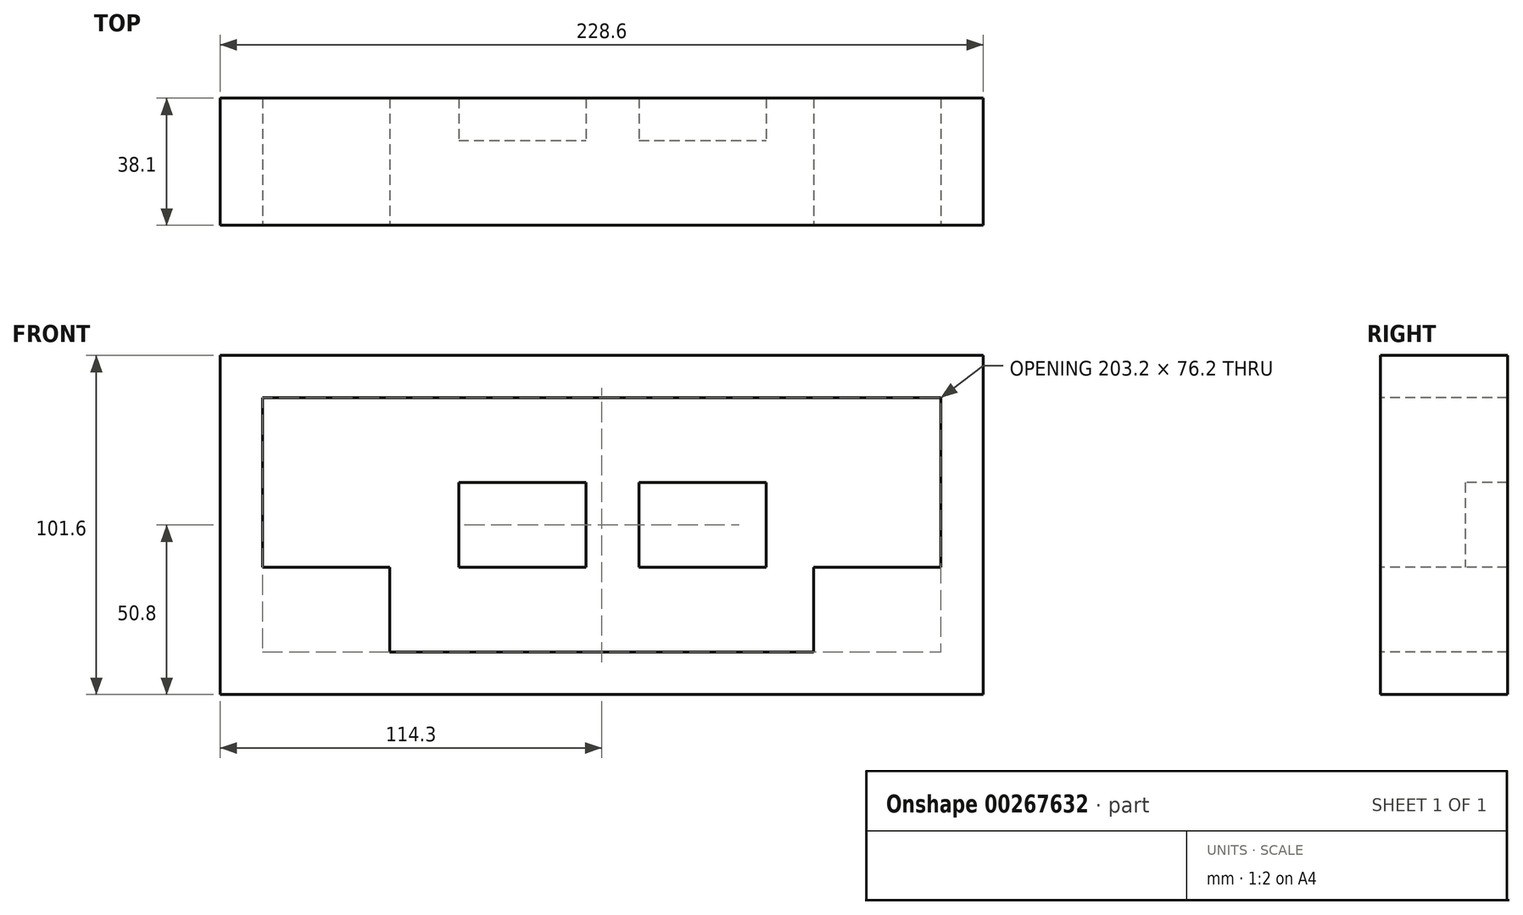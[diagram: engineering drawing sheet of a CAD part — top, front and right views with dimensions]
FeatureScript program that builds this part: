
annotation { "Feature Type Name" : "Feature", "Feature Type Description" : "" }
export const myFeature = defineFeature(function(context is Context, id is Id, definition is map)
    precondition{}
    {
        {
            var Q0;
            Q0=qCreatedBy(makeId("Front.planeOp"),FACE);
            var sketch = newSketch(context, id + "F0", { "sketchPlane" : qUnion([Q0])});
            skPoint(sketch, "E0.middle", {"position": v(0, 0) * mm});
            skLineSegment(sketch, "E1.bottom", {"start": v(-114.3, -50.8) * mm, "end": v(114.3, -50.8) * mm});
            skLineSegment(sketch, "E1.top", {"start": v(-114.3, 50.8) * mm, "end": v(114.3, 50.8) * mm});
            skLineSegment(sketch, "E1.left", {"start": v(-114.3, -50.8) * mm, "end": v(-114.3, 50.8) * mm});
            skLineSegment(sketch, "E1.right", {"start": v(114.3, -50.8) * mm, "end": v(114.3, 50.8) * mm});
            skLineSegment(sketch, "E2.bottom", {"start": v(-101.6, -38.1) * mm, "end": v(101.6, -38.1) * mm});
            skLineSegment(sketch, "E2.top", {"start": v(-101.6, 38.1) * mm, "end": v(101.6, 38.1) * mm});
            skLineSegment(sketch, "E2.left", {"start": v(-101.6, -38.1) * mm, "end": v(-101.6, 38.1) * mm});
            skLineSegment(sketch, "E2.right", {"start": v(101.6, -38.1) * mm, "end": v(101.6, 38.1) * mm});
            skLineSegment(sketch, "E3.bottom", {"start": v(-101.6, 38.1) * mm, "end": v(-62.18, 38.1) * mm});
            skLineSegment(sketch, "E3.top", {"start": v(-101.6, 12.7) * mm, "end": v(-62.18, 12.7) * mm});
            skLineSegment(sketch, "E3.left", {"start": v(-101.6, 38.1) * mm, "end": v(-101.6, 12.7) * mm});
            skLineSegment(sketch, "E3.right", {"start": v(-62.18, 38.1) * mm, "end": v(-62.18, 12.7) * mm});
            skLineSegment(sketch, "E4.bottom", {"start": v(-101.6, -38.1) * mm, "end": v(-63.5, -38.1) * mm});
            skLineSegment(sketch, "E4.top", {"start": v(-101.6, -12.7) * mm, "end": v(-63.5, -12.7) * mm});
            skLineSegment(sketch, "E4.left", {"start": v(-101.6, -38.1) * mm, "end": v(-101.6, -12.7) * mm});
            skLineSegment(sketch, "E4.right", {"start": v(-63.5, -38.1) * mm, "end": v(-63.5, -12.7) * mm});
            skLineSegment(sketch, "E5.bottom", {"start": v(101.6, -38.1) * mm, "end": v(63.5, -38.1) * mm});
            skLineSegment(sketch, "E5.top", {"start": v(101.6, -12.7) * mm, "end": v(63.5, -12.7) * mm});
            skLineSegment(sketch, "E5.left", {"start": v(101.6, -38.1) * mm, "end": v(101.6, -12.7) * mm});
            skLineSegment(sketch, "E5.right", {"start": v(63.5, -38.1) * mm, "end": v(63.5, -12.7) * mm});
            skLineSegment(sketch, "E6.bottom", {"start": v(101.6, 38.1) * mm, "end": v(63.5, 38.1) * mm});
            skLineSegment(sketch, "E6.top", {"start": v(101.6, 12.7) * mm, "end": v(63.5, 12.7) * mm});
            skLineSegment(sketch, "E6.left", {"start": v(101.6, 38.1) * mm, "end": v(101.6, 12.7) * mm});
            skLineSegment(sketch, "E6.right", {"start": v(63.5, 38.1) * mm, "end": v(63.5, 12.7) * mm});
            skLineSegment(sketch, "E7.bottom", {"start": v(-42.84, 12.7) * mm, "end": v(-4.74, 12.7) * mm});
            skLineSegment(sketch, "E7.top", {"start": v(-42.84, -12.7) * mm, "end": v(-4.74, -12.7) * mm});
            skLineSegment(sketch, "E7.left", {"start": v(-42.84, 12.7) * mm, "end": v(-42.84, -12.7) * mm});
            skLineSegment(sketch, "E7.right", {"start": v(-4.74, 12.7) * mm, "end": v(-4.74, -12.7) * mm});
            skPoint(sketch, "E7.middle", {"position": v(-23.8, 0) * mm});
            skLineSegment(sketch, "E8.bottom", {"start": v(11.17, 12.7) * mm, "end": v(49.27, 12.7) * mm});
            skLineSegment(sketch, "E8.top", {"start": v(11.17, -12.7) * mm, "end": v(49.27, -12.7) * mm});
            skLineSegment(sketch, "E8.left", {"start": v(11.17, 12.7) * mm, "end": v(11.17, -12.7) * mm});
            skLineSegment(sketch, "E8.right", {"start": v(49.27, 12.7) * mm, "end": v(49.27, -12.7) * mm});
            skPoint(sketch, "E8.middle", {"position": v(30.22, 0) * mm});
            skSolve(sketch);
        }
        {
            var Q0;
            Q0=makeQuery(id+"F0.imprint","IMPRINT",FACE,{"disambiguationData":[TD([[makeQuery(id+"F0.imprint","IMPRINT",EDGE,{"derivedFrom":sQuery(id+"F0.wireOp",EDGE,"E1.bottom")}),1.0]])]});
            var Q1;
            Q1=makeQuery(id+"F0.imprint","IMPRINT",FACE,{"disambiguationData":[TD([[makeQuery(id+"F0.imprint","IMPRINT",EDGE,{"derivedFrom":sQuery(id+"F0.wireOp",EDGE,"E3.bottom")}),-1.0]])]});
            var Q2;
            Q2=makeQuery(id+"F0.imprint","IMPRINT",FACE,{"disambiguationData":[TD([[makeQuery(id+"F0.imprint","IMPRINT",EDGE,{"derivedFrom":sQuery(id+"F0.wireOp",EDGE,"E2.bottom")}),1.0]])]});
            var Q3;
            Q3=makeQuery(id+"F0.imprint","IMPRINT",FACE,{"disambiguationData":[TD([[makeQuery(id+"F0.imprint","IMPRINT",EDGE,{"derivedFrom":sQuery(id+"F0.wireOp",EDGE,"E7.bottom")}),-1.0]])]});
            var Q4;
            Q4=makeQuery(id+"F0.imprint","IMPRINT",FACE,{"disambiguationData":[TD([[makeQuery(id+"F0.imprint","IMPRINT",EDGE,{"derivedFrom":sQuery(id+"F0.wireOp",EDGE,"E4.bottom")}),1.0]])]});
            var Q5;
            Q5=makeQuery(id+"F0.imprint","IMPRINT",FACE,{"disambiguationData":[TD([[makeQuery(id+"F0.imprint","IMPRINT",EDGE,{"derivedFrom":sQuery(id+"F0.wireOp",EDGE,"E8.bottom")}),-1.0]])]});
            var Q6;
            Q6=makeQuery(id+"F0.imprint","IMPRINT",FACE,{"disambiguationData":[TD([[makeQuery(id+"F0.imprint","IMPRINT",EDGE,{"derivedFrom":sQuery(id+"F0.wireOp",EDGE,"E5.bottom")}),-1.0]])]});
            var Q7;
            Q7=makeQuery(id+"F0.imprint","IMPRINT",FACE,{"disambiguationData":[TD([[makeQuery(id+"F0.imprint","IMPRINT",EDGE,{"derivedFrom":sQuery(id+"F0.wireOp",EDGE,"E6.bottom")}),1.0]])]});
            extrude(context, id + "F1", {"entities" : qUnion([Q0, Q1, Q2, Q3, Q4, Q5, Q6, Q7]), "oppositeDirection" : true, "depth" : 38.1 * mm});
        }
        {
            var Q0;
            Q0=makeQuery(id+"F0.imprint","IMPRINT",FACE,{"disambiguationData":[TD([[makeQuery(id+"F0.imprint","IMPRINT",EDGE,{"derivedFrom":sQuery(id+"F0.wireOp",EDGE,"E3.bottom")}),-1.0]])]});
            var Q1;
            Q1=makeQuery(id+"F0.imprint","IMPRINT",FACE,{"disambiguationData":[TD([[makeQuery(id+"F0.imprint","IMPRINT",EDGE,{"derivedFrom":sQuery(id+"F0.wireOp",EDGE,"E4.bottom")}),1.0]])]});
            var Q2;
            Q2=makeQuery(id+"F0.imprint","IMPRINT",FACE,{"disambiguationData":[TD([[makeQuery(id+"F0.imprint","IMPRINT",EDGE,{"derivedFrom":sQuery(id+"F0.wireOp",EDGE,"E7.bottom")}),-1.0]])]});
            var Q3;
            Q3=makeQuery(id+"F0.imprint","IMPRINT",FACE,{"disambiguationData":[TD([[makeQuery(id+"F0.imprint","IMPRINT",EDGE,{"derivedFrom":sQuery(id+"F0.wireOp",EDGE,"E8.bottom")}),-1.0]])]});
            var Q4;
            Q4=makeQuery(id+"F0.imprint","IMPRINT",FACE,{"disambiguationData":[TD([[makeQuery(id+"F0.imprint","IMPRINT",EDGE,{"derivedFrom":sQuery(id+"F0.wireOp",EDGE,"E6.bottom")}),1.0]])]});
            var Q5;
            Q5=makeQuery(id+"F0.imprint","IMPRINT",FACE,{"disambiguationData":[TD([[makeQuery(id+"F0.imprint","IMPRINT",EDGE,{"derivedFrom":sQuery(id+"F0.wireOp",EDGE,"E5.bottom")}),-1.0]])]});
            extrude(context, id + "F2", {"entities" : qUnion([Q0, Q1, Q2, Q3, Q4, Q5]), "operationType" : NewBodyOperationType.REMOVE, "oppositeDirection" : true, "depth" : 25.4 * mm});
        }
    });
